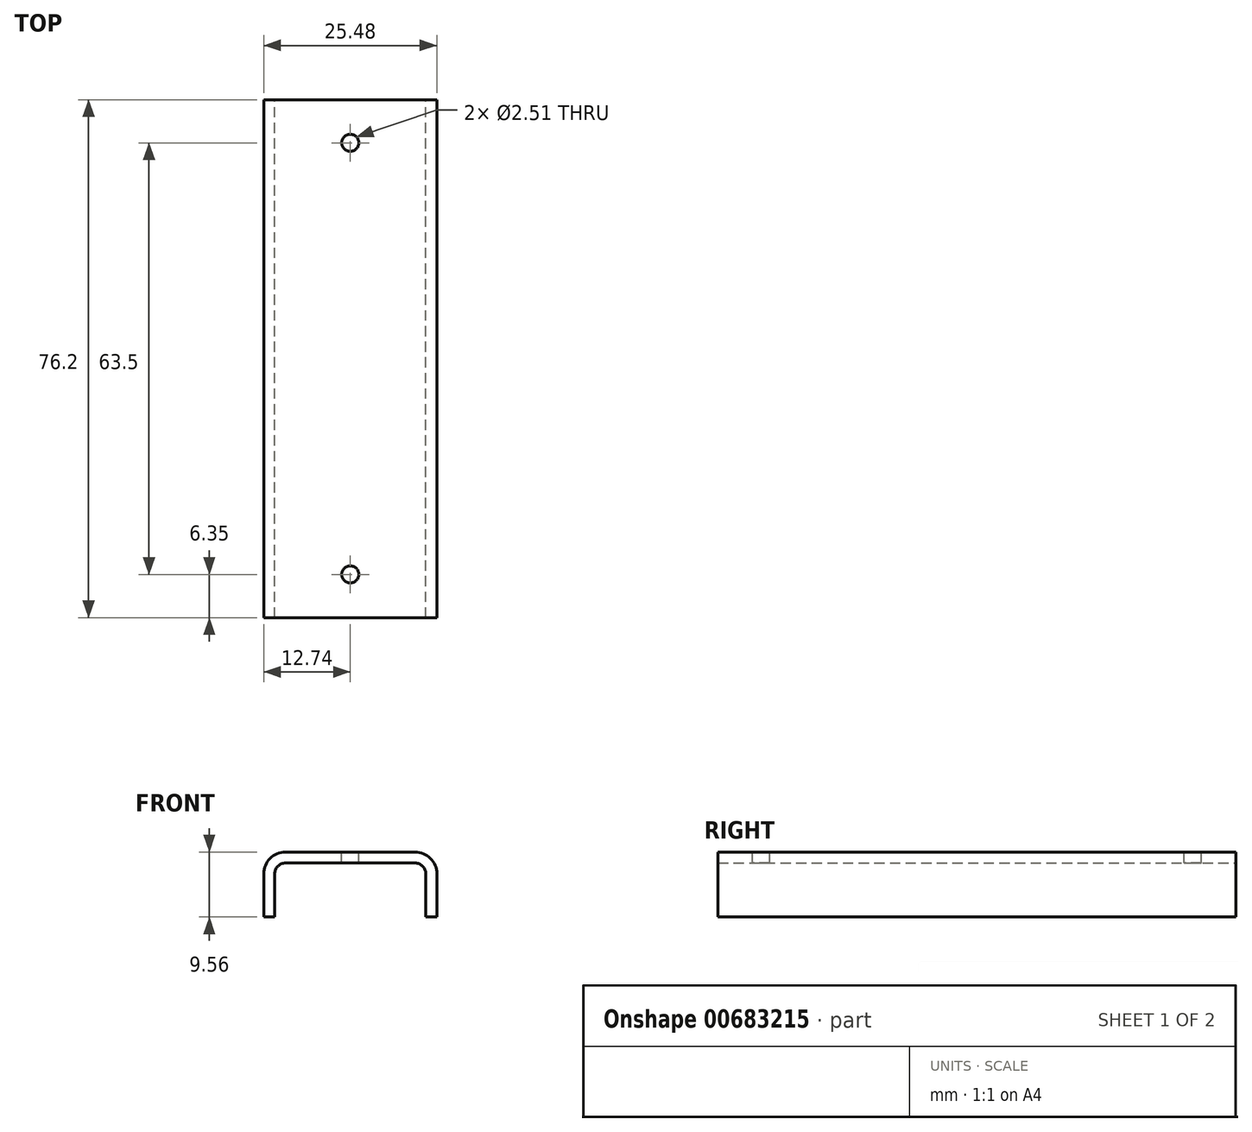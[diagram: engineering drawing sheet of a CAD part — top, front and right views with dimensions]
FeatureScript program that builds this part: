
annotation { "Feature Type Name" : "Feature", "Feature Type Description" : "" }
export const myFeature = defineFeature(function(context is Context, id is Id, definition is map)
    precondition{}
    {
        {
            var Q0;
            Q0=qCreatedBy(makeId("Front.planeOp"),FACE);
            var sketch = newSketch(context, id + "F0", { "sketchPlane" : qUnion([Q0])});
            skLineSegment(sketch, "E0", {"start": v(-12.74, 0) * mm, "end": v(-11.11, 0) * mm});
            skLineSegment(sketch, "E1", {"start": v(-11.11, 0) * mm, "end": v(-11.11, 6.35) * mm});
            skLineSegment(sketch, "E2", {"start": v(-9.53, 7.94) * mm, "end": v(9.53, 7.94) * mm});
            skLineSegment(sketch, "E3", {"start": v(11.11, 6.35) * mm, "end": v(11.11, 0) * mm});
            skLineSegment(sketch, "E4", {"start": v(11.11, 0) * mm, "end": v(12.74, 0) * mm});
            skLineSegment(sketch, "E5", {"start": v(12.74, 0) * mm, "end": v(12.74, 6.35) * mm});
            skLineSegment(sketch, "E6", {"start": v(9.53, 9.56) * mm, "end": v(-9.53, 9.56) * mm});
            skLineSegment(sketch, "E7", {"start": v(-12.74, 6.35) * mm, "end": v(-12.74, 0) * mm});
            skPoint(sketch, "E8.visualSharp", {"position": v(-11.11, 7.94) * mm});
            skArc(sketch, "E8.filletArc", {"start": v(-9.53, 7.94) * mm, "mid": v(-10.65, 7.47) * mm, "end": v(-11.11, 6.35) * mm});
            skPoint(sketch, "E9.visualSharp", {"position": v(11.11, 7.94) * mm});
            skArc(sketch, "E9.filletArc", {"start": v(11.11, 6.35) * mm, "mid": v(10.65, 7.47) * mm, "end": v(9.53, 7.94) * mm});
            skPoint(sketch, "E10.visualSharp", {"position": v(-12.74, 9.56) * mm});
            skArc(sketch, "E10.filletArc", {"start": v(-9.53, 9.56) * mm, "mid": v(-11.8, 8.62) * mm, "end": v(-12.74, 6.35) * mm});
            skPoint(sketch, "E11.visualSharp", {"position": v(12.74, 9.56) * mm});
            skArc(sketch, "E11.filletArc", {"start": v(12.74, 6.35) * mm, "mid": v(11.8, 8.62) * mm, "end": v(9.53, 9.56) * mm});
            skSolve(sketch);
        }
        {
            var Q0;
            Q0=makeQuery(id+"F0.imprint","IMPRINT",FACE,{"disambiguationData":[TD([[makeQuery(id+"F0.imprint","IMPRINT",EDGE,{"derivedFrom":sQuery(id+"F0.wireOp",EDGE,"E0")}),1.0]])]});
            extrude(context, id + "F1", {"entities" : qUnion([Q0]), "endBound" : BoundingType.SYMMETRIC, "depth" : 76.2 * mm, "offsetDistance" : 25.4 * mm});
        }
        {
            var Q0;
            Q0=makeQuery(id+"F1.opExtrude","SWEPT_FACE",FACE,{"disambiguationData":[OSD([sQuery(id+"F0.wireOp",EDGE,"E6")])]});
            var sketch = newSketch(context, id + "F2", { "sketchPlane" : qUnion([Q0])});
            skCircle(sketch, "E12", {"center": v(0, 31.75) * mm, "radius": 1.26 * mm});
            skCircle(sketch, "E13", {"center": v(0, -31.75) * mm, "radius": 1.26 * mm});
            skSolve(sketch);
        }
        {
            var Q0;
            Q0=makeQuery(id+"F2.imprint","IMPRINT",FACE,{"disambiguationData":[TD([[makeQuery(id+"F2.imprint","IMPRINT",EDGE,{"derivedFrom":sQuery(id+"F2.wireOp",EDGE,"E12")}),1.0]])]});
            var Q1;
            Q1=makeQuery(id+"F2.imprint","IMPRINT",FACE,{"disambiguationData":[TD([[makeQuery(id+"F2.imprint","IMPRINT",EDGE,{"derivedFrom":sQuery(id+"F2.wireOp",EDGE,"E13")}),1.0]])]});
            extrude(context, id + "F3", {"entities" : qUnion([Q0, Q1]), "operationType" : NewBodyOperationType.REMOVE, "endBound" : BoundingType.UP_TO_NEXT, "oppositeDirection" : true, "depth" : 25.4 * mm, "offsetDistance" : 25.4 * mm});
        }
    });
